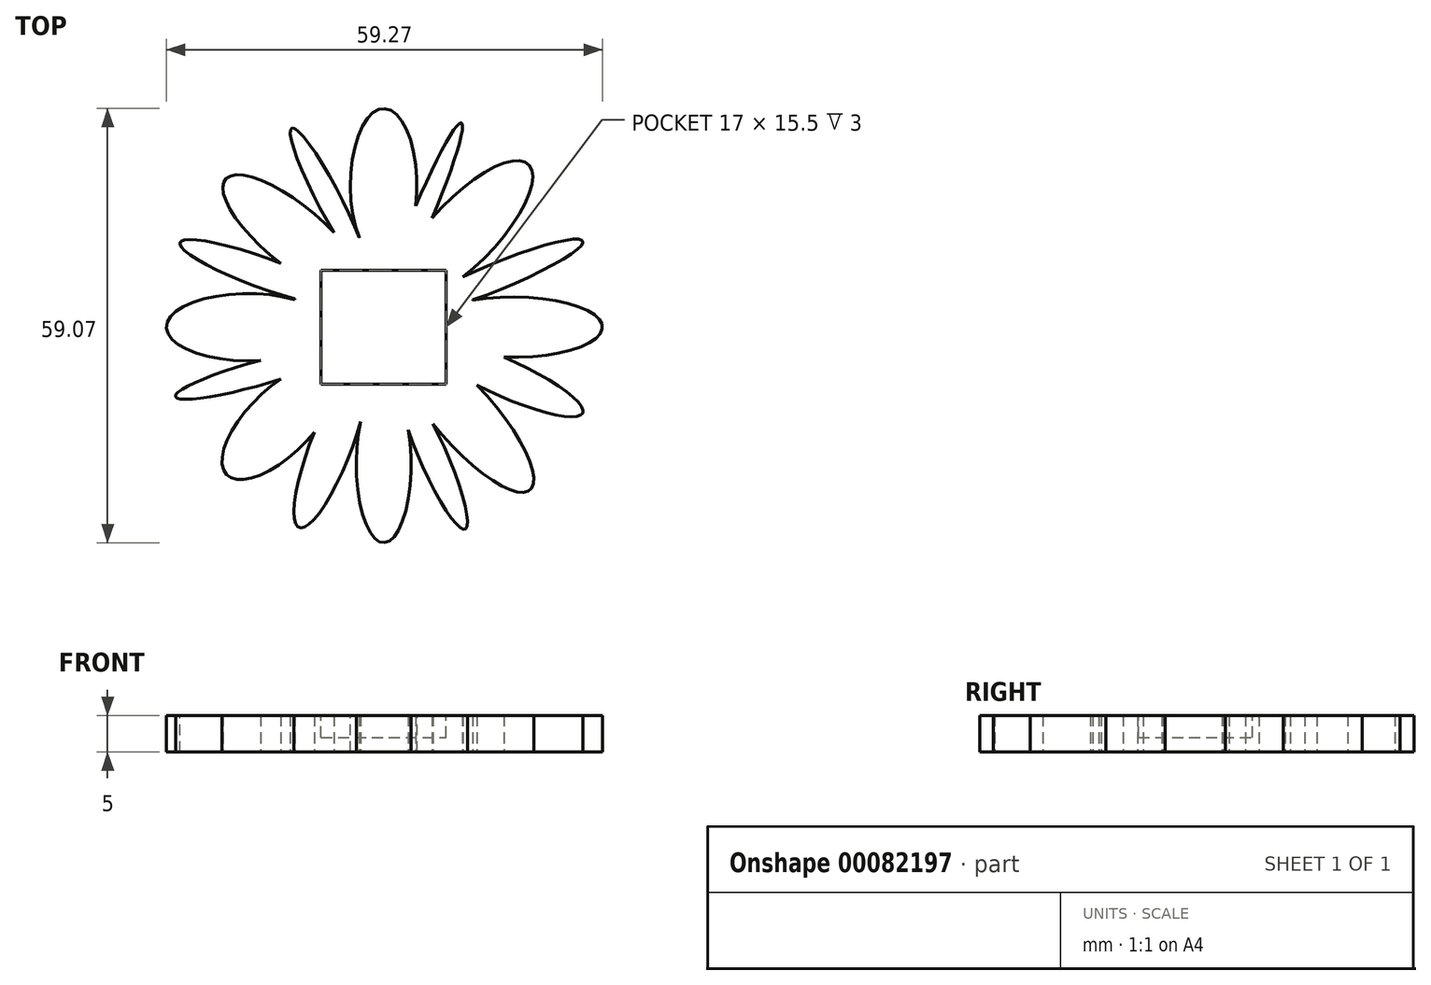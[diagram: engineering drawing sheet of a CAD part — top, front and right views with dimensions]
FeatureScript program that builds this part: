
annotation { "Feature Type Name" : "Feature", "Feature Type Description" : "" }
export const myFeature = defineFeature(function(context is Context, id is Id, definition is map)
    precondition{}
    {
        {
            var Q0;
            Q0=qCreatedBy(makeId("Top.planeOp"),FACE);
            var sketch = newSketch(context, id + "F0", { "sketchPlane" : qUnion([Q0])});
            skCircle(sketch, "E0", {"center": v(0, 0) * mm, "radius": 12.5 * mm});
            skEllipse(sketch, "E1", {"center": v(0, 19.28) * mm, "majorRadius": 10.46 * mm, "minorRadius": 4.53 * mm, "majorAxis": v(0, 1)});
            skEllipse(sketch, "E2", {"center": v(0, -18.66) * mm, "majorRadius": 10.66 * mm, "minorRadius": 3.72 * mm, "majorAxis": v(0, -1)});
            skEllipse(sketch, "E3", {"center": v(17.64, 0) * mm, "majorRadius": 12.1 * mm, "minorRadius": 4.1 * mm, "majorAxis": v(1, 0)});
            skEllipse(sketch, "E4", {"center": v(-18.46, 0) * mm, "majorRadius": 11.07 * mm, "minorRadius": 4.58 * mm, "majorAxis": v(-1, 0)});
            skEllipse(sketch, "E5", {"center": v(-14.15, -12.92) * mm, "majorRadius": 10.15 * mm, "minorRadius": 4.44 * mm, "majorAxis": v(-0.7, -0.7)});
            skEllipse(sketch, "E6", {"center": v(11.07, -12.1) * mm, "majorRadius": 13.37 * mm, "minorRadius": 4.04 * mm, "majorAxis": v(0.66, -0.75)});
            skEllipse(sketch, "E7", {"center": v(11.07, 13.13) * mm, "majorRadius": 12.47 * mm, "minorRadius": 4.47 * mm, "majorAxis": v(0.7, 0.72)});
            skEllipse(sketch, "E8", {"center": v(-12.3, 12.5) * mm, "majorRadius": 11.95 * mm, "minorRadius": 4.07 * mm, "majorAxis": v(-0.77, 0.64)});
            skEllipse(sketch, "E9", {"center": v(-7.59, 17.64) * mm, "majorRadius": 10.64 * mm, "minorRadius": 1.6 * mm, "majorAxis": v(-0.46, 0.89)});
            skEllipse(sketch, "E10", {"center": v(-16.4, 7.38) * mm, "majorRadius": 12 * mm, "minorRadius": 2.05 * mm, "majorAxis": v(-0.94, 0.34)});
            skEllipse(sketch, "E11", {"center": v(-17.29, -6.36) * mm, "majorRadius": 11.43 * mm, "minorRadius": 1.63 * mm, "majorAxis": v(-0.96, -0.27)});
            skPoint(sketch, "E11.centerSnap0", {"position": v(-17.29, -9.78) * mm});
            skEllipse(sketch, "E12", {"center": v(-7.18, -16.2) * mm, "majorRadius": 11.88 * mm, "minorRadius": 2.79 * mm, "majorAxis": v(-0.36, -0.93)});
            skEllipse(sketch, "E13", {"center": v(6.77, -17.64) * mm, "majorRadius": 10.74 * mm, "minorRadius": 1.87 * mm, "majorAxis": v(0.4, -0.92)});
            skEllipse(sketch, "E14", {"center": v(16.2, -6.77) * mm, "majorRadius": 11.93 * mm, "minorRadius": 2.53 * mm, "majorAxis": v(0.91, -0.41)});
            skEllipse(sketch, "E15", {"center": v(15.59, 6.97) * mm, "majorRadius": 12.42 * mm, "minorRadius": 1.82 * mm, "majorAxis": v(0.93, 0.38)});
            skEllipse(sketch, "E16", {"center": v(5.43, 15.55) * mm, "majorRadius": 13.3 * mm, "minorRadius": 1.35 * mm, "majorAxis": v(0.39, 0.92)});
            skCircle(sketch, "E17", {"center": v(0, 0) * mm, "radius": 12.47 * mm});
            skSolve(sketch);
        }
        {
            var Q0;
            Q0=qSketchRegion(id+"F0",true);
            extrude(context, id + "F1", {"entities" : qUnion([Q0]), "depth" : 5 * mm});
        }
        {
            var Q0;
            Q0=qCreatedBy(makeId("Top.planeOp"),FACE);
            var sketch = newSketch(context, id + "F2", { "sketchPlane" : qUnion([Q0])});
            skCircle(sketch, "E18", {"center": v(0, 0) * mm, "radius": 12.66 * mm});
            skSolve(sketch);
        }
        {
            var Q0;
            Q0=qSketchRegion(id+"F2",true);
            extrude(context, id + "F3", {"entities" : qUnion([Q0]), "operationType" : NewBodyOperationType.ADD, "depth" : 5 * mm});
        }
        {
            var Q0;
            Q0=makeQuery(id+"F3.boolean.opBoolean","MERGE",FACE,{"derivedFrom":[makeQuery(id+"F1.opExtrude","CAP_FACE",FACE,{"disambiguationData":[OSD([sQuery(id+"F0.wireOp",EDGE,"E0"),sQuery(id+"F0.wireOp",EDGE,"E1"),sQuery(id+"F0.wireOp",EDGE,"E2"),sQuery(id+"F0.wireOp",EDGE,"E3"),sQuery(id+"F0.wireOp",EDGE,"E4"),sQuery(id+"F0.wireOp",EDGE,"E5"),sQuery(id+"F0.wireOp",EDGE,"E6"),sQuery(id+"F0.wireOp",EDGE,"E7"),sQuery(id+"F0.wireOp",EDGE,"E8"),sQuery(id+"F0.wireOp",EDGE,"E9"),sQuery(id+"F0.wireOp",EDGE,"E10"),sQuery(id+"F0.wireOp",EDGE,"E11"),sQuery(id+"F0.wireOp",EDGE,"E12"),sQuery(id+"F0.wireOp",EDGE,"E13"),sQuery(id+"F0.wireOp",EDGE,"E14"),sQuery(id+"F0.wireOp",EDGE,"E15"),sQuery(id+"F0.wireOp",EDGE,"E16"),sQuery(id+"F0.wireOp",EDGE,"E17")])],"isStart":false}),makeQuery(id+"F3.opExtrude","CAP_FACE",FACE,{"disambiguationData":[OSD([sQuery(id+"F2.wireOp",EDGE,"E18")])],"isStart":false})]});
            var sketch = newSketch(context, id + "F4", { "sketchPlane" : qUnion([Q0])});
            skLineSegment(sketch, "E19.bottom", {"start": v(-8.5, -7.75) * mm, "end": v(8.5, -7.75) * mm});
            skLineSegment(sketch, "E19.top", {"start": v(-8.5, 7.75) * mm, "end": v(8.5, 7.75) * mm});
            skLineSegment(sketch, "E19.left", {"start": v(-8.5, -7.75) * mm, "end": v(-8.5, 7.75) * mm});
            skLineSegment(sketch, "E19.right", {"start": v(8.5, -7.75) * mm, "end": v(8.5, 7.75) * mm});
            skPoint(sketch, "E19.middle", {"position": v(0, 0) * mm});
            skSolve(sketch);
        }
        {
            var Q0;
            Q0=qSketchRegion(id+"F4",true);
            extrude(context, id + "F5", {"entities" : qUnion([Q0]), "operationType" : NewBodyOperationType.REMOVE, "oppositeDirection" : true, "depth" : 3 * mm});
        }
    });
